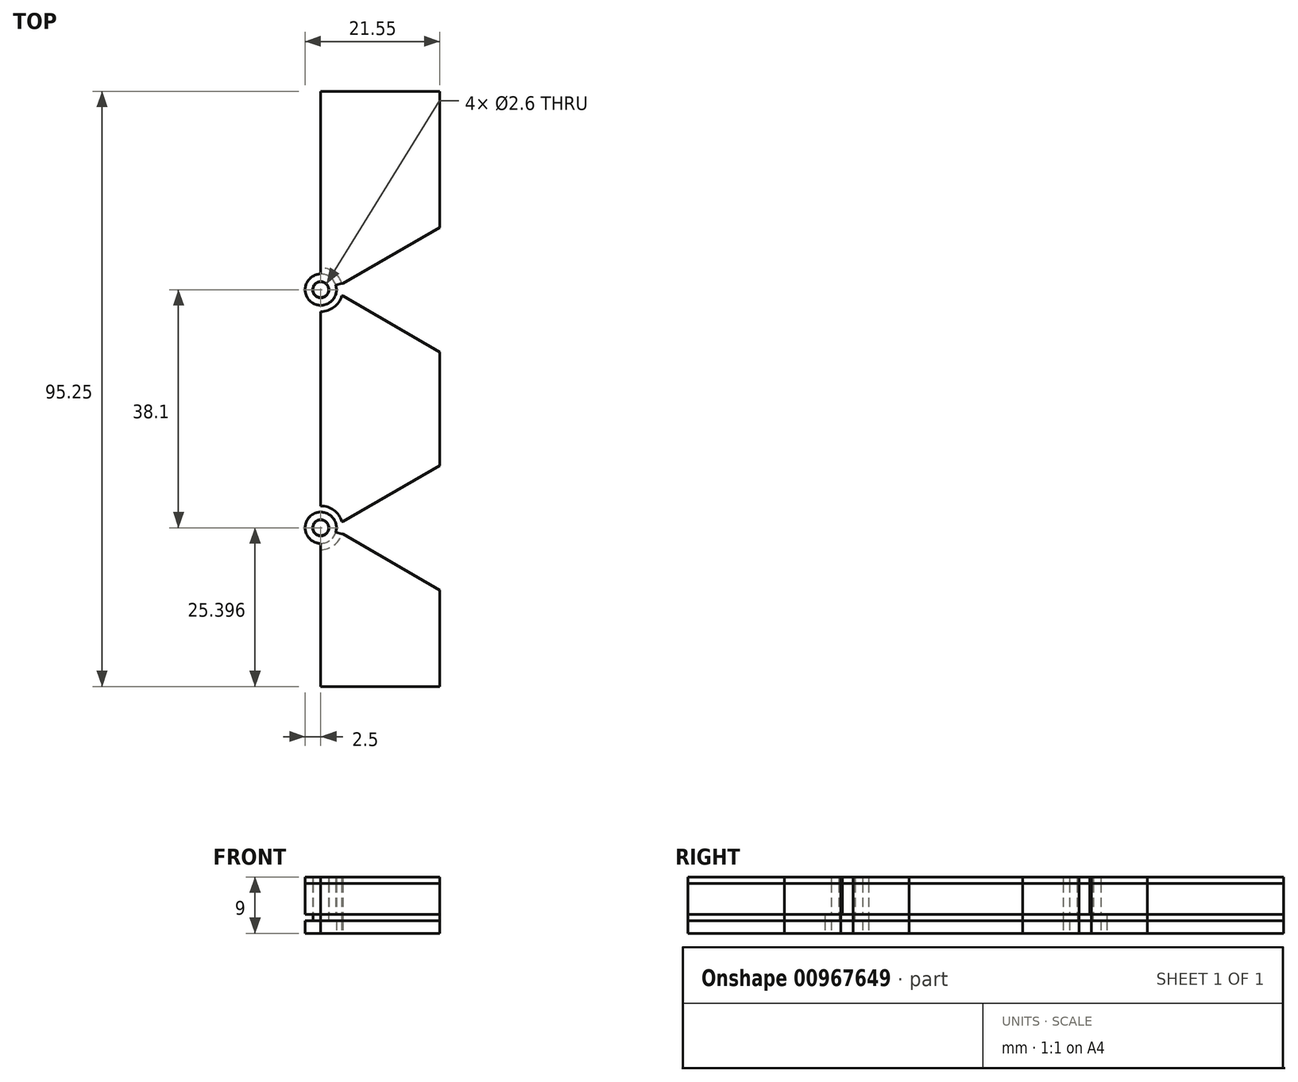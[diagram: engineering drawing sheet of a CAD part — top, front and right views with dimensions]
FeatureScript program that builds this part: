
annotation { "Feature Type Name" : "Feature", "Feature Type Description" : "" }
export const myFeature = defineFeature(function(context is Context, id is Id, definition is map)
    precondition{}
    {
        {
            var Q0;
            Q0=qCreatedBy(makeId("Top.planeOp"),FACE);
            var sketch = newSketch(context, id + "F0", { "sketchPlane" : qUnion([Q0])});
            skLineSegment(sketch, "E0.bottom", {"start": v(-19.05, 49.56) * mm, "end": v(0, 49.56) * mm});
            skLineSegment(sketch, "E0.left", {"start": v(-19.05, 49.56) * mm, "end": v(-19.05, 21.3) * mm});
            skLineSegment(sketch, "E0.right", {"start": v(0, 49.56) * mm, "end": v(0, 27.78) * mm});
            skLineSegment(sketch, "E1.right", {"start": v(0, 7.83) * mm, "end": v(0, -10.32) * mm});
            skLineSegment(sketch, "E2.top", {"start": v(-19.05, -45.7) * mm, "end": v(0, -45.7) * mm});
            skLineSegment(sketch, "E2.right", {"start": v(0, -30.27) * mm, "end": v(0, -45.7) * mm});
            skCircle(sketch, "E3", {"center": v(-19.05, 17.8) * mm, "radius": 2.5 * mm});
            skCircle(sketch, "E4", {"center": v(-19.05, -20.3) * mm, "radius": 2.5 * mm});
            skArc(sketch, "E5.0", {"start": v(-19.05, 14.3) * mm, "mid": v(-16.96, 15) * mm, "end": v(-15.7, 16.8) * mm});
            skArc(sketch, "E6.0", {"start": v(-19.05, -23.8) * mm, "mid": v(-16.96, -23.1) * mm, "end": v(-15.7, -21.3) * mm});
            skLineSegment(sketch, "E7.trimOffspring", {"start": v(-19.05, -23.8) * mm, "end": v(-19.05, -45.7) * mm});
            skLineSegment(sketch, "E8.trimOffspring", {"start": v(-19.05, 14.3) * mm, "end": v(-19.05, -16.8) * mm});
            skLineSegment(sketch, "E9.0", {"start": v(0, -21.3) * mm, "end": v(0, -21.3) * mm});
            skLineSegment(sketch, "E10", {"start": v(-15.55, 18.8) * mm, "end": v(-15.7, 18.8) * mm});
            skLineSegment(sketch, "E11", {"start": v(-15.55, 16.8) * mm, "end": v(-15.7, 16.8) * mm});
            skArc(sketch, "E12.trimOffspring", {"start": v(-15.7, 18.8) * mm, "mid": v(-16.96, 20.61) * mm, "end": v(-19.05, 21.3) * mm});
            skPoint(sketch, "E13.orphan", {"position": v(0, 17.8) * mm});
            skLineSegment(sketch, "E14", {"start": v(-15.55, -19.3) * mm, "end": v(-15.7, -19.3) * mm});
            skLineSegment(sketch, "E15", {"start": v(-15.55, -21.3) * mm, "end": v(-15.7, -21.3) * mm});
            skArc(sketch, "E16.trimOffspring", {"start": v(-15.7, -19.3) * mm, "mid": v(-16.96, -17.49) * mm, "end": v(-19.05, -16.8) * mm});
            skPoint(sketch, "E17.trimOffspring.end.orphan", {"position": v(0, -20.3) * mm});
            skLineSegment(sketch, "E18", {"start": v(-15.55, 18.8) * mm, "end": v(0, 27.78) * mm});
            skLineSegment(sketch, "E19", {"start": v(-15.55, 16.8) * mm, "end": v(0, 7.83) * mm});
            skLineSegment(sketch, "E20", {"start": v(-15.55, -19.3) * mm, "end": v(0, -10.32) * mm});
            skLineSegment(sketch, "E21", {"start": v(-15.55, -21.3) * mm, "end": v(0, -30.27) * mm});
            skSolve(sketch);
        }
        {
            var Q0;
            Q0 = qSketchRegion(id + "F0", true);
            extrude(context, id + "F1", {"entities" : qUnion([Q0]), "depth" : 2 * mm, "offsetDistance" : 25.4 * mm});
        }
        {
            var Q0;
            Q0=makeQuery(id+"F1.opExtrude","CAP_FACE",FACE,{"disambiguationData":[OSD([sQuery(id+"F0.wireOp",EDGE,"E0.bottom"),sQuery(id+"F0.wireOp",EDGE,"E0.left"),sQuery(id+"F0.wireOp",EDGE,"E0.right"),sQuery(id+"F0.wireOp",EDGE,"E10"),sQuery(id+"F0.wireOp",EDGE,"E12.trimOffspring"),sQuery(id+"F0.wireOp",EDGE,"E18")])],"isStart":false});
            var sketch = newSketch(context, id + "F2", { "sketchPlane" : qUnion([Q0])});
            skLineSegment(sketch, "E22.0.0", {"start": v(-15.7, 18.8) * mm, "end": v(-15.55, 18.8) * mm});
            skLineSegment(sketch, "E22.0.1", {"start": v(-15.55, 18.8) * mm, "end": v(0, 27.78) * mm});
            skLineSegment(sketch, "E22.0.2", {"start": v(0, 27.78) * mm, "end": v(0, 49.56) * mm});
            skLineSegment(sketch, "E22.0.3", {"start": v(0, 49.56) * mm, "end": v(-19.05, 49.56) * mm});
            skLineSegment(sketch, "E22.0.4", {"start": v(-19.05, 49.56) * mm, "end": v(-19.05, 21.3) * mm});
            skArc(sketch, "E22.0.5", {"start": v(-19.05, 21.3) * mm, "mid": v(-16.96, 20.61) * mm, "end": v(-15.7, 18.8) * mm});
            skArc(sketch, "E23.0.0", {"start": v(-15.7, 16.8) * mm, "mid": v(-16.96, 15) * mm, "end": v(-19.05, 14.3) * mm});
            skLineSegment(sketch, "E23.0.1", {"start": v(-19.05, 14.3) * mm, "end": v(-19.05, -16.8) * mm});
            skArc(sketch, "E23.0.2", {"start": v(-19.05, -16.8) * mm, "mid": v(-16.96, -17.49) * mm, "end": v(-15.7, -19.3) * mm});
            skLineSegment(sketch, "E23.0.3", {"start": v(-15.7, -19.3) * mm, "end": v(-15.55, -19.3) * mm});
            skLineSegment(sketch, "E23.0.4", {"start": v(-15.55, -19.3) * mm, "end": v(0, -10.32) * mm});
            skLineSegment(sketch, "E23.0.5", {"start": v(0, -10.32) * mm, "end": v(0, 7.83) * mm});
            skLineSegment(sketch, "E23.0.6", {"start": v(0, 7.83) * mm, "end": v(-15.55, 16.8) * mm});
            skLineSegment(sketch, "E23.0.7", {"start": v(-15.55, 16.8) * mm, "end": v(-15.7, 16.8) * mm});
            skLineSegment(sketch, "E24.0.0", {"start": v(0, -30.27) * mm, "end": v(-15.55, -21.3) * mm});
            skLineSegment(sketch, "E24.0.1", {"start": v(-15.55, -21.3) * mm, "end": v(-15.7, -21.3) * mm});
            skArc(sketch, "E24.0.2", {"start": v(-15.7, -21.3) * mm, "mid": v(-16.96, -23.1) * mm, "end": v(-19.05, -23.8) * mm});
            skLineSegment(sketch, "E24.0.3", {"start": v(-19.05, -23.8) * mm, "end": v(-19.05, -45.7) * mm});
            skLineSegment(sketch, "E24.0.4", {"start": v(-19.05, -45.7) * mm, "end": v(0, -45.7) * mm});
            skLineSegment(sketch, "E24.0.5", {"start": v(0, -45.7) * mm, "end": v(0, -30.27) * mm});
            skCircle(sketch, "E25", {"center": v(-19.05, 17.8) * mm, "radius": 1.25 * mm});
            skCircle(sketch, "E26", {"center": v(-19.05, -20.3) * mm, "radius": 1.25 * mm});
            skSolve(sketch);
        }
        {
            var Q0;
            Q0 = qSketchRegion(id + "F2", true);
            extrude(context, id + "F3", {"entities" : qUnion([Q0]), "depth" : 1 * mm, "offsetDistance" : 25.4 * mm});
        }
        {
            var Q0;
            Q0=makeQuery(id+"F3.opExtrude","CAP_FACE",FACE,{"disambiguationData":[OSD([sQuery(id+"F2.wireOp",EDGE,"E22.0.0"),sQuery(id+"F2.wireOp",EDGE,"E22.0.1"),sQuery(id+"F2.wireOp",EDGE,"E22.0.2"),sQuery(id+"F2.wireOp",EDGE,"E22.0.3"),sQuery(id+"F2.wireOp",EDGE,"E22.0.4"),sQuery(id+"F2.wireOp",EDGE,"E22.0.5")])],"isStart":false});
            var sketch = newSketch(context, id + "F4", { "sketchPlane" : qUnion([Q0])});
            skLineSegment(sketch, "E27.0.0", {"start": v(-15.7, 18.8) * mm, "end": v(-15.55, 18.8) * mm});
            skLineSegment(sketch, "E27.0.1", {"start": v(-15.55, 18.8) * mm, "end": v(0, 27.78) * mm});
            skLineSegment(sketch, "E27.0.2", {"start": v(0, 27.78) * mm, "end": v(0, 49.56) * mm});
            skLineSegment(sketch, "E27.0.3", {"start": v(0, 49.56) * mm, "end": v(-19.05, 49.56) * mm});
            skLineSegment(sketch, "E27.0.4", {"start": v(-19.05, 49.56) * mm, "end": v(-19.05, 21.3) * mm});
            skCircle(sketch, "E28.0.0", {"center": v(-19.05, 17.8) * mm, "radius": 1.25 * mm});
            skLineSegment(sketch, "E29.0.0", {"start": v(0, 7.83) * mm, "end": v(-15.55, 16.8) * mm});
            skLineSegment(sketch, "E29.0.1", {"start": v(-15.55, 16.8) * mm, "end": v(-15.7, 16.8) * mm});
            skArc(sketch, "E29.0.2", {"start": v(-15.7, 16.8) * mm, "mid": v(-16.96, 15) * mm, "end": v(-19.05, 14.3) * mm});
            skLineSegment(sketch, "E29.0.3", {"start": v(-19.05, 14.3) * mm, "end": v(-19.05, -16.8) * mm});
            skArc(sketch, "E29.0.4", {"start": v(-19.05, -16.8) * mm, "mid": v(-16.96, -17.49) * mm, "end": v(-15.7, -19.3) * mm});
            skLineSegment(sketch, "E29.0.5", {"start": v(-15.7, -19.3) * mm, "end": v(-15.55, -19.3) * mm});
            skLineSegment(sketch, "E29.0.6", {"start": v(-15.55, -19.3) * mm, "end": v(0, -10.32) * mm});
            skLineSegment(sketch, "E29.0.7", {"start": v(0, -10.32) * mm, "end": v(0, 7.83) * mm});
            skLineSegment(sketch, "E30.0.0", {"start": v(-19.05, -45.7) * mm, "end": v(0, -45.7) * mm});
            skLineSegment(sketch, "E30.0.1", {"start": v(0, -45.7) * mm, "end": v(0, -30.27) * mm});
            skLineSegment(sketch, "E30.0.2", {"start": v(0, -30.27) * mm, "end": v(-15.55, -21.3) * mm});
            skLineSegment(sketch, "E30.0.3", {"start": v(-15.55, -21.3) * mm, "end": v(-15.7, -21.3) * mm});
            skLineSegment(sketch, "E30.0.5", {"start": v(-19.05, -23.8) * mm, "end": v(-19.05, -45.7) * mm});
            skCircle(sketch, "E31.0", {"center": v(-19.05, -20.3) * mm, "radius": 1.25 * mm});
            skCircle(sketch, "E32", {"center": v(-19.05, 17.8) * mm, "radius": 1.3 * mm});
            skArc(sketch, "E33", {"start": v(-19.05, 20.3) * mm, "mid": v(-20.54, 15.8) * mm, "end": v(-16.65, 18.52) * mm});
            skCircle(sketch, "E34", {"center": v(-19.05, -20.3) * mm, "radius": 1.3 * mm});
            skArc(sketch, "E35", {"start": v(-16.65, -21) * mm, "mid": v(-20.54, -18.29) * mm, "end": v(-19.05, -22.8) * mm});
            skLineSegment(sketch, "E36", {"start": v(-15.7, 18.8) * mm, "end": v(-16.65, 18.52) * mm});
            skLineSegment(sketch, "E37", {"start": v(-19.05, 21.3) * mm, "end": v(-19.05, 20.3) * mm});
            skLineSegment(sketch, "E38", {"start": v(-15.7, -21.3) * mm, "end": v(-16.65, -21) * mm});
            skLineSegment(sketch, "E39", {"start": v(-19.05, -23.8) * mm, "end": v(-19.05, -22.8) * mm});
            skSolve(sketch);
        }
        {
            var Q0;
            Q0 = qSketchRegion(id + "F4", true);
            var Q1;
            Q1=makeQuery(id+"F4.imprint","IMPRINT",FACE,{"disambiguationData":[TD([[makeQuery(id+"F4.imprint","IMPRINT",EDGE,{"derivedFrom":sQuery(id+"F4.wireOp",EDGE,"E28.0.0")}),1.0]])]});
            var Q2;
            Q2=makeQuery(id+"F4.imprint","IMPRINT",FACE,{"disambiguationData":[TD([[makeQuery(id+"F4.imprint","IMPRINT",EDGE,{"derivedFrom":sQuery(id+"F4.wireOp",EDGE,"E31.0")}),1.0]])]});
            extrude(context, id + "F5", {"entities" : qUnion([Q0, Q1, Q2]), "depth" : 5 * mm, "offsetDistance" : 25.4 * mm});
        }
        {
            var Q0;
            Q0=makeQuery(id+"F5.opExtrude","CAP_FACE",FACE,{"disambiguationData":[OSD([sQuery(id+"F4.wireOp",EDGE,"E28.0.0")])],"isStart":false});
            var Q1;
            Q1=makeQuery(id+"F5.opExtrude","CAP_FACE",FACE,{"disambiguationData":[OSD([sQuery(id+"F4.wireOp",EDGE,"E31.0")])],"isStart":false});
            var Q2;
            Q2=makeQuery(id+"F5.opExtrude","CAP_FACE",FACE,{"disambiguationData":[OSD([sQuery(id+"F4.wireOp",EDGE,"E27.0.0"),sQuery(id+"F4.wireOp",EDGE,"E27.0.1"),sQuery(id+"F4.wireOp",EDGE,"E27.0.2"),sQuery(id+"F4.wireOp",EDGE,"E27.0.3"),sQuery(id+"F4.wireOp",EDGE,"E27.0.4"),sQuery(id+"F4.wireOp",EDGE,"E27.0.5")])],"isStart":false});
            var Q3;
            Q3=makeQuery(id+"F5.opExtrude","CAP_FACE",FACE,{"disambiguationData":[OSD([sQuery(id+"F4.wireOp",EDGE,"E29.0.0"),sQuery(id+"F4.wireOp",EDGE,"E29.0.1"),sQuery(id+"F4.wireOp",EDGE,"E29.0.2"),sQuery(id+"F4.wireOp",EDGE,"E29.0.3"),sQuery(id+"F4.wireOp",EDGE,"E29.0.4"),sQuery(id+"F4.wireOp",EDGE,"E29.0.5"),sQuery(id+"F4.wireOp",EDGE,"E29.0.6"),sQuery(id+"F4.wireOp",EDGE,"E29.0.7")])],"isStart":false});
            var Q4;
            Q4=makeQuery(id+"F5.opExtrude","CAP_FACE",FACE,{"disambiguationData":[OSD([sQuery(id+"F4.wireOp",EDGE,"E30.0.0"),sQuery(id+"F4.wireOp",EDGE,"E30.0.1"),sQuery(id+"F4.wireOp",EDGE,"E30.0.2"),sQuery(id+"F4.wireOp",EDGE,"E30.0.3"),sQuery(id+"F4.wireOp",EDGE,"E30.0.4"),sQuery(id+"F4.wireOp",EDGE,"E30.0.5")])],"isStart":false});
            extrude(context, id + "F6", {"entities" : qUnion([Q0, Q1, Q2, Q3, Q4]), "depth" : 1 * mm, "offsetDistance" : 25.4 * mm});
        }
    });
